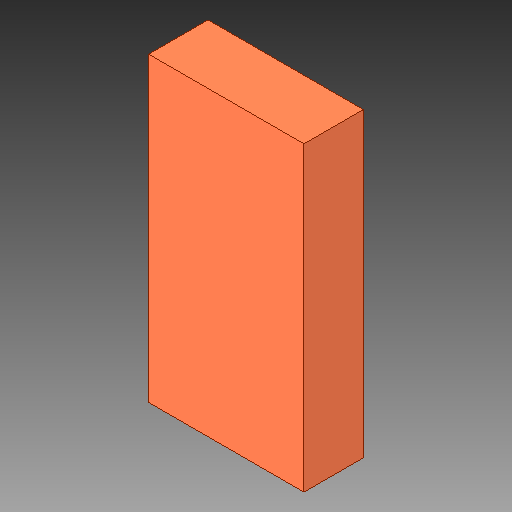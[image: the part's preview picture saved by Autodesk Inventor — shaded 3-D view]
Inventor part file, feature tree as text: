
AUTODESK INVENTOR PART (.ipt)
format: ipt  version: 2018 (Build 220112000, 112)  size: 79,872 bytes
history: native  units: in
note: dims shown in document units (in); Inventor stores cm internally (conversion verified against a paired STEP export)
features: other x1, extrude x1
ambient origin geometry x8: Origin, YZ Plane, XZ Plane, XY Plane, X Axis, Y Axis, Z Axis, Center Point
bodies: Solid1 (feature_tree)
feature tree (2):
  other  "JP1, LED1_PWR_79"
  extrude  "Extrusion1"  Depth=0.0394in TaperAngle=0.0deg
